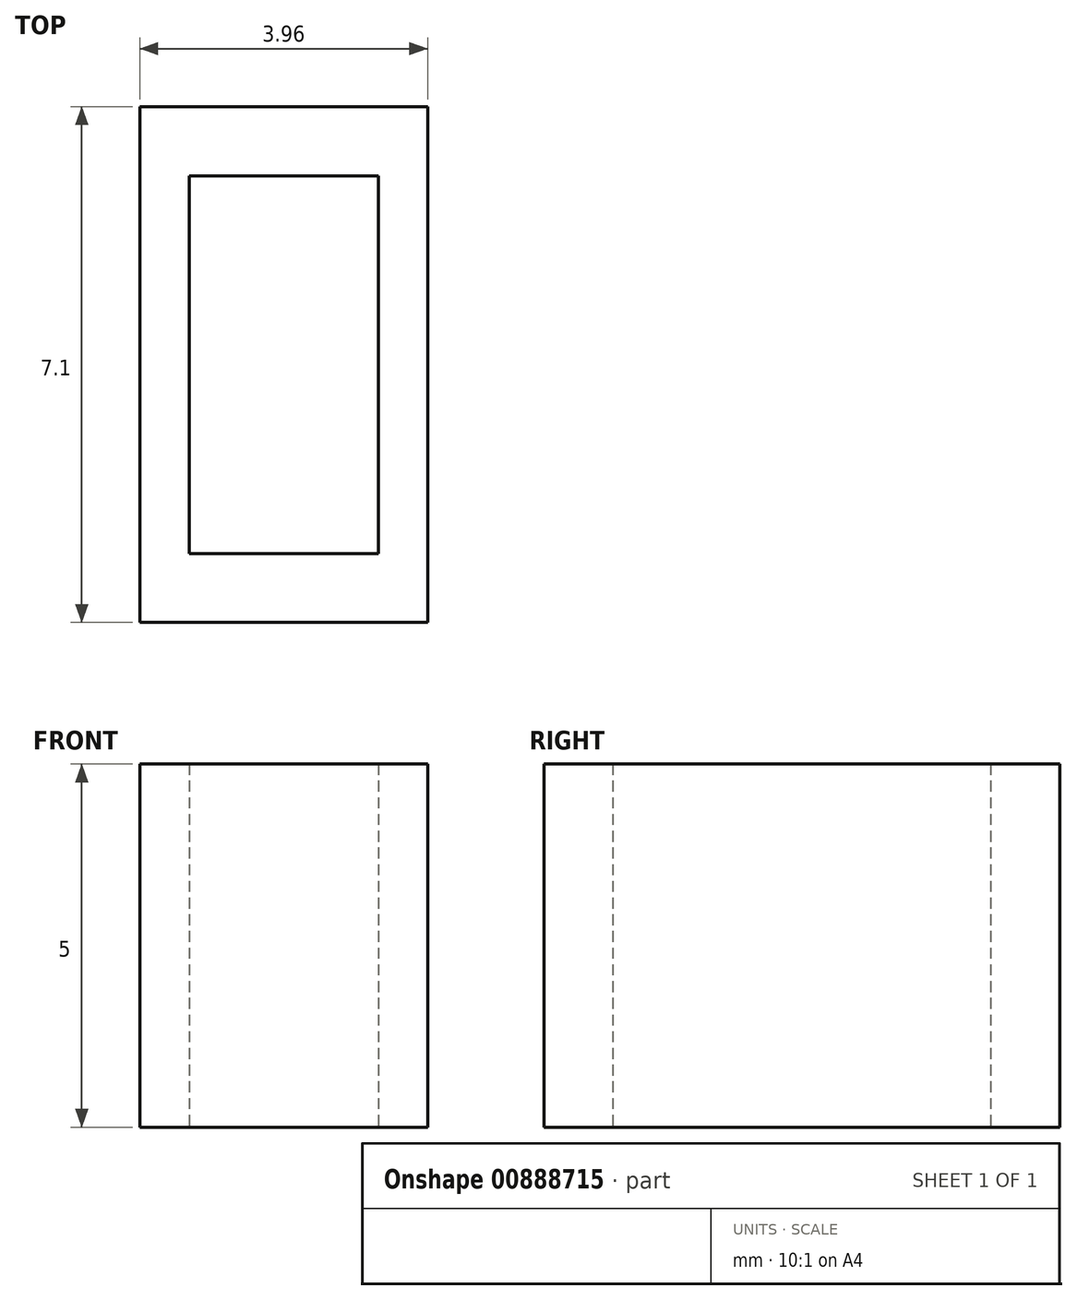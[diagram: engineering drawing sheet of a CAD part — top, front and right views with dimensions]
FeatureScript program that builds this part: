
annotation { "Feature Type Name" : "Feature", "Feature Type Description" : "" }
export const myFeature = defineFeature(function(context is Context, id is Id, definition is map)
    precondition{}
    {
        {
            var Q0;
            Q0=qCreatedBy(makeId("Top.planeOp"),FACE);
            var sketch = newSketch(context, id + "F0", { "sketchPlane" : qUnion([Q0])});
            skLineSegment(sketch, "E0.bottom", {"start": v(1.14, 2.6) * mm, "end": v(-1.46, 2.6) * mm});
            skLineSegment(sketch, "E0.top", {"start": v(1.14, -2.6) * mm, "end": v(-1.46, -2.6) * mm});
            skLineSegment(sketch, "E0.left", {"start": v(1.14, 2.6) * mm, "end": v(1.14, -2.6) * mm});
            skLineSegment(sketch, "E0.right", {"start": v(-1.46, 2.6) * mm, "end": v(-1.46, -2.6) * mm});
            skPoint(sketch, "E0.middle", {"position": v(-0.16, 0) * mm});
            skLineSegment(sketch, "E1.bottom", {"start": v(1.82, 3.55) * mm, "end": v(-2.14, 3.55) * mm});
            skLineSegment(sketch, "E1.top", {"start": v(1.82, -3.55) * mm, "end": v(-2.14, -3.55) * mm});
            skLineSegment(sketch, "E1.left", {"start": v(1.82, 3.55) * mm, "end": v(1.82, -3.55) * mm});
            skLineSegment(sketch, "E1.right", {"start": v(-2.14, 3.55) * mm, "end": v(-2.14, -3.55) * mm});
            skSolve(sketch);
        }
        {
            var Q0;
            Q0 = qSketchRegion(id + "F0", true);
            extrude(context, id + "F1", {"entities" : qUnion([Q0]), "depth" : 5 * mm, "offsetDistance" : 25 * mm});
        }
    });
